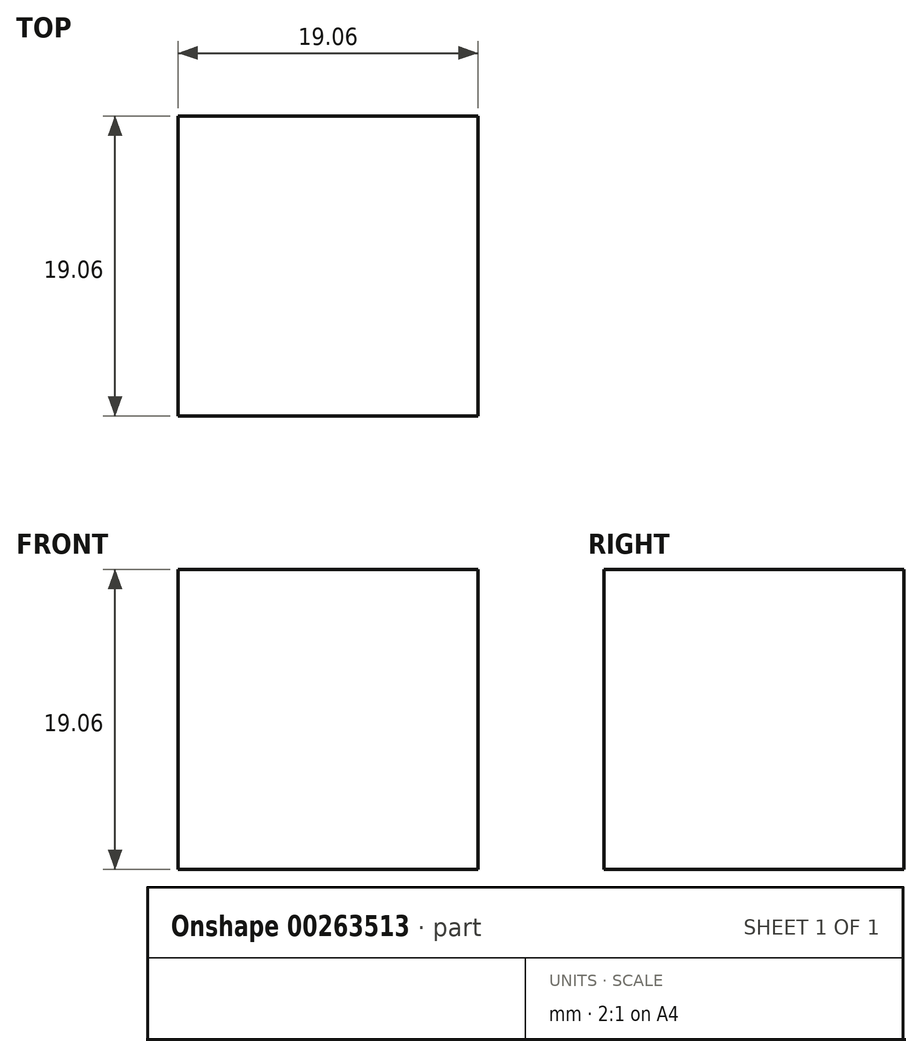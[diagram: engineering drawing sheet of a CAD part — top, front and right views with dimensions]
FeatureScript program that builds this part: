
annotation { "Feature Type Name" : "Feature", "Feature Type Description" : "" }
export const myFeature = defineFeature(function(context is Context, id is Id, definition is map)
    precondition{}
    {
        {
            var Q0;
            Q0=qCreatedBy(makeId("Front.planeOp"),FACE);
            var sketch = newSketch(context, id + "F0", { "sketchPlane" : qUnion([Q0])});
            skLineSegment(sketch, "E0.bottom", {"start": v(9.53, 9.52) * mm, "end": v(-9.52, 9.52) * mm});
            skLineSegment(sketch, "E0.top", {"start": v(9.53, -9.52) * mm, "end": v(-9.53, -9.52) * mm});
            skLineSegment(sketch, "E0.left", {"start": v(9.53, 9.52) * mm, "end": v(9.53, -9.52) * mm});
            skLineSegment(sketch, "E0.right", {"start": v(-9.52, 9.52) * mm, "end": v(-9.53, -9.52) * mm});
            skPoint(sketch, "E0.middle", {"position": v(0, 0) * mm});
            skSolve(sketch);
        }
        {
            var Q0;
            Q0=makeQuery(id+"F0.imprint","IMPRINT",FACE,{"disambiguationData":[TD([[makeQuery(id+"F0.imprint","IMPRINT",EDGE,{"derivedFrom":sQuery(id+"F0.wireOp",EDGE,"E0.bottom")}),1.0]])]});
            extrude(context, id + "F1", {"entities" : qUnion([Q0]), "endBound" : BoundingType.SYMMETRIC, "depth" : 19.05 * mm});
        }
    });
